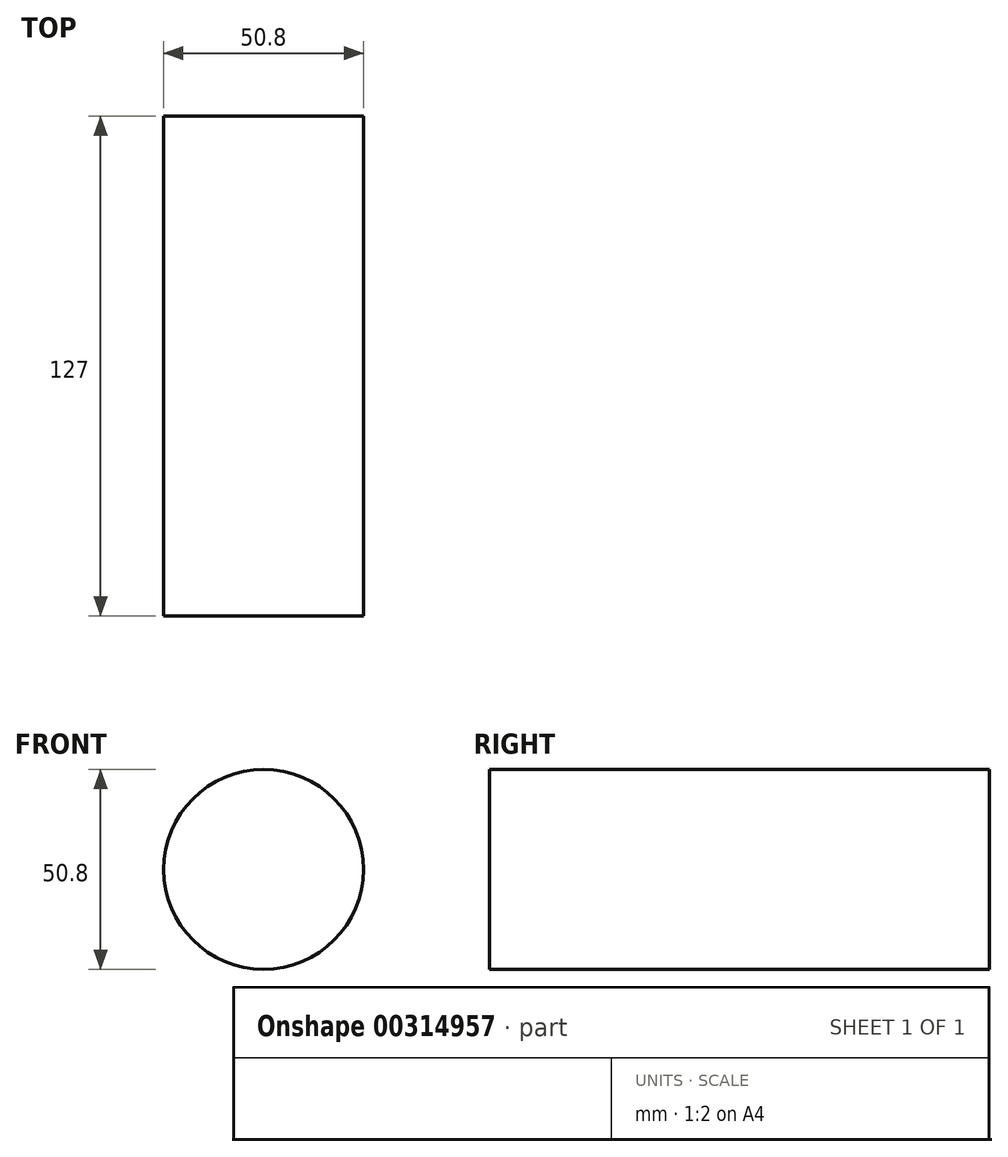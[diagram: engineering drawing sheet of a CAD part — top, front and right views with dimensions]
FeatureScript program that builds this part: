
annotation { "Feature Type Name" : "Feature", "Feature Type Description" : "" }
export const myFeature = defineFeature(function(context is Context, id is Id, definition is map)
    precondition{}
    {
        {
            var Q0;
            Q0=qCreatedBy(makeId("Front.planeOp"),FACE);
            var sketch = newSketch(context, id + "F0", { "sketchPlane" : qUnion([Q0])});
            skCircle(sketch, "E0", {"center": v(0, 0) * mm, "radius": 25.4 * mm});
            skSolve(sketch);
        }
        {
            var Q0;
            Q0=makeQuery(id+"F0.imprint","IMPRINT",FACE,{"disambiguationData":[TD([[makeQuery(id+"F0.imprint","IMPRINT",EDGE,{"derivedFrom":sQuery(id+"F0.wireOp",EDGE,"E0")}),1.0]])]});
            extrude(context, id + "F1", {"entities" : qUnion([Q0]), "endBound" : BoundingType.SYMMETRIC, "depth" : 127 * mm});
        }
    });
